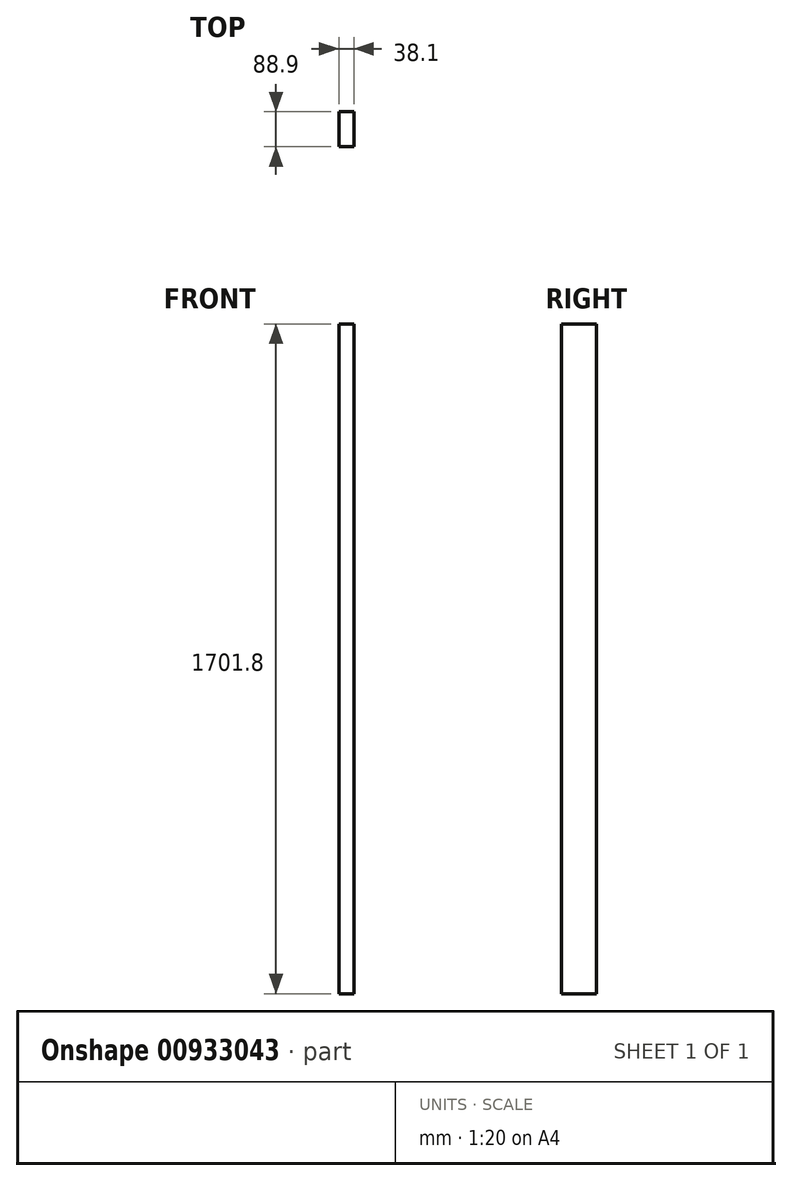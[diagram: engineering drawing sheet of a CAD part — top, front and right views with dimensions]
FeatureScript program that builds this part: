
annotation { "Feature Type Name" : "Feature", "Feature Type Description" : "" }
export const myFeature = defineFeature(function(context is Context, id is Id, definition is map)
    precondition{}
    {
        {
            var Q0;
            Q0=qCreatedBy(makeId("Top.planeOp"),FACE);
            var sketch = newSketch(context, id + "F0", { "sketchPlane" : qUnion([Q0])});
            skLineSegment(sketch, "E0.bottom", {"start": v(19.05, 44.45) * mm, "end": v(-19.05, 44.45) * mm});
            skLineSegment(sketch, "E0.top", {"start": v(19.05, -44.45) * mm, "end": v(-19.05, -44.45) * mm});
            skLineSegment(sketch, "E0.left", {"start": v(19.05, 44.45) * mm, "end": v(19.05, -44.45) * mm});
            skLineSegment(sketch, "E0.right", {"start": v(-19.05, 44.45) * mm, "end": v(-19.05, -44.45) * mm});
            skPoint(sketch, "E0.middle", {"position": v(0, 0) * mm});
            skSolve(sketch);
        }
        {
            var Q0;
            Q0=makeQuery(id+"F0.imprint","IMPRINT",FACE,{"disambiguationData":[TD([[makeQuery(id+"F0.imprint","IMPRINT",EDGE,{"derivedFrom":sQuery(id+"F0.wireOp",EDGE,"E0.bottom")}),1.0]])]});
            extrude(context, id + "F1", {"entities" : qUnion([Q0]), "depth" : 1701.8 * mm, "offsetDistance" : 25.4 * mm});
        }
    });
